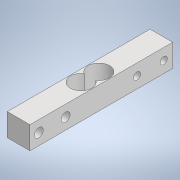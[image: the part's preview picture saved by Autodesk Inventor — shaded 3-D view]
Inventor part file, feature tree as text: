
AUTODESK INVENTOR PART (.ipt)
format: ipt  version: 2021 (Build 250183000, 183)  size: 171,520 bytes
history: native  units: mm
features: thread x4, extrude x2, sketch x2, other x1, chamfer x1
ambient origin geometry x8: Origin, YZ Plane, XZ Plane, XY Plane, X Axis, Y Axis, Z Axis, Center Point
bodies: Body1 (feature_tree)
feature tree (10):
  other  "Bryła1"
  extrude  "Wyciągnięcie proste1"  Depth=12.7mm
  extrude  "Wyciągnięcie proste2"  Depth=80.0mm
  thread  "Gwint1"
  thread  "Gwint2"
  thread  "Gwint3"
  thread  "Gwint4"
  chamfer  "Faza1"  Distance=4.0mm
  sketch  "Szkic1"
  sketch  "Szkic2"
